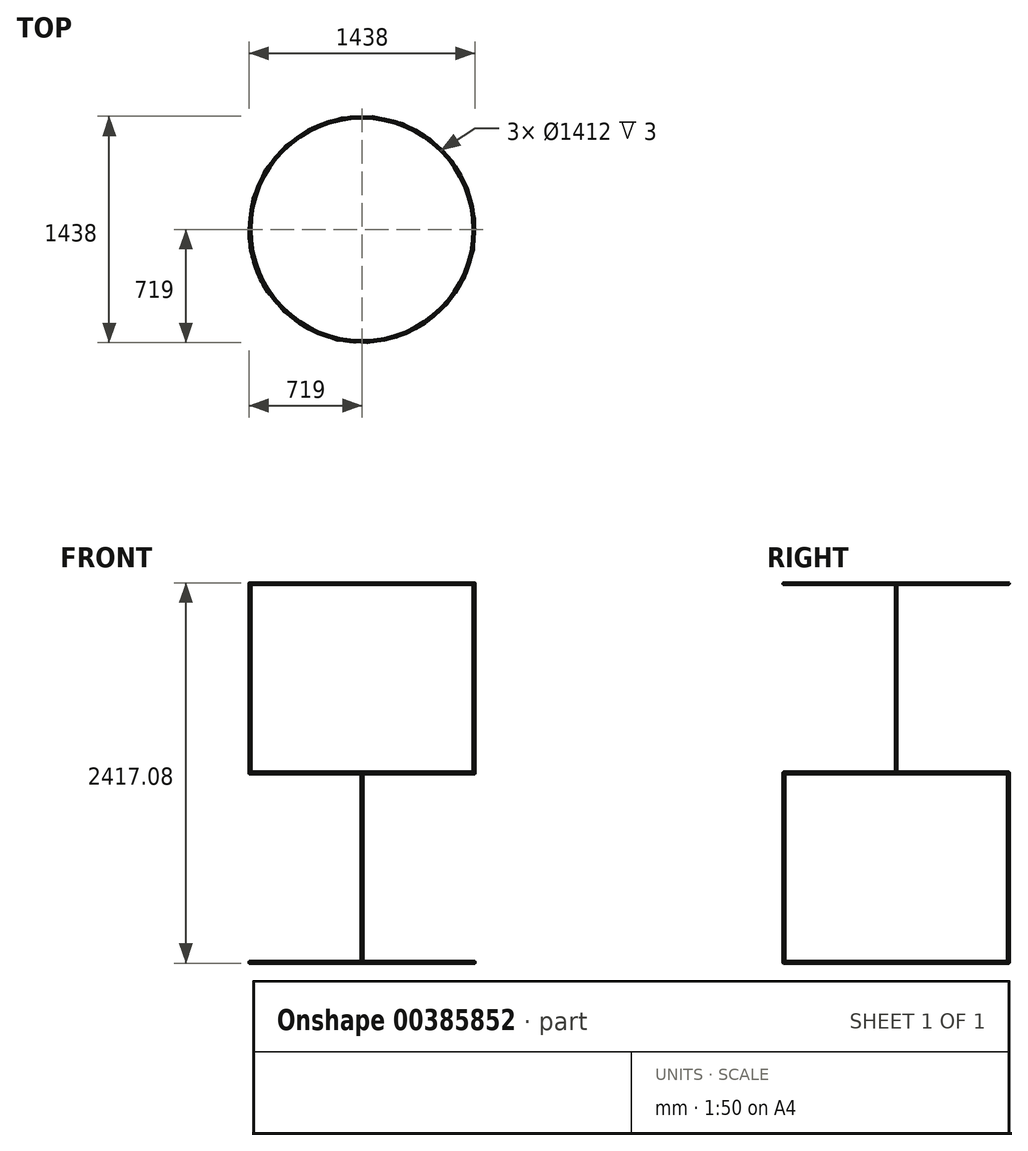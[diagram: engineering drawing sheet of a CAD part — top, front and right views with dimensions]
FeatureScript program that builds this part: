
annotation { "Feature Type Name" : "Feature", "Feature Type Description" : "" }
export const myFeature = defineFeature(function(context is Context, id is Id, definition is map)
    precondition{}
    {
        {
            var Q0;
            Q0=qCreatedBy(makeId("Front.planeOp"),FACE);
            var sketch = newSketch(context, id + "F0", { "sketchPlane" : qUnion([Q0])});
            skLineSegment(sketch, "E0", {"start": v(0, 0) * mm, "end": v(716, 0) * mm, "construction": true});
            skLineSegment(sketch, "E1", {"start": v(0, 0) * mm, "end": v(0, 347.59) * mm, "construction": true});
            skLineSegment(sketch, "E2", {"start": v(706, 1.5) * mm, "end": v(706, -1.5) * mm});
            skLineSegment(sketch, "E3", {"start": v(706, 1.5) * mm, "end": v(709, 1.5) * mm});
            skLineSegment(sketch, "E4", {"start": v(709, 1.5) * mm, "end": v(716, 5.54) * mm});
            skLineSegment(sketch, "E5", {"start": v(716, 0) * mm, "end": v(716, 5.54) * mm, "construction": true});
            skLineSegment(sketch, "E6", {"start": v(716, 0) * mm, "end": v(719, 0) * mm, "construction": true});
            skLineSegment(sketch, "E7.MirrorCS", {"start": v(706, -1.5) * mm, "end": v(709, -1.5) * mm});
            skLineSegment(sketch, "E8.MirrorCS", {"start": v(709, -1.5) * mm, "end": v(716, -5.54) * mm});
            skArc(sketch, "E9", {"start": v(716, -5.54) * mm, "mid": v(719, 0) * mm, "end": v(716, 5.54) * mm});
            skLineSegment(sketch, "E10.0.1.0", {"start": v(709, 1204.5) * mm, "end": v(716, 1208.54) * mm});
            skLineSegment(sketch, "E10.0.1.1", {"start": v(706, 1204.5) * mm, "end": v(709, 1204.5) * mm});
            skLineSegment(sketch, "E10.0.1.2", {"start": v(706, 1204.5) * mm, "end": v(706, 1201.5) * mm});
            skLineSegment(sketch, "E10.0.1.3", {"start": v(706, 1201.5) * mm, "end": v(709, 1201.5) * mm});
            skLineSegment(sketch, "E10.0.1.4", {"start": v(709, 1201.5) * mm, "end": v(716, 1197.46) * mm});
            skArc(sketch, "E10.0.1.5", {"start": v(716, 1197.46) * mm, "mid": v(719, 1203) * mm, "end": v(716, 1208.54) * mm});
            skLineSegment(sketch, "E10.direction1", {"start": v(709, 1.5) * mm, "end": v(734, 1.5) * mm, "construction": true});
            skLineSegment(sketch, "E10.direction2", {"start": v(709, 1.5) * mm, "end": v(709, 1204.5) * mm, "construction": true});
            skLineSegment(sketch, "E11.MirrorCS", {"start": v(706, -1201.5) * mm, "end": v(709, -1201.5) * mm});
            skLineSegment(sketch, "E12.MirrorCS", {"start": v(709, -1201.5) * mm, "end": v(716, -1197.46) * mm});
            skLineSegment(sketch, "E13.MirrorCS", {"start": v(706, -1204.5) * mm, "end": v(709, -1204.5) * mm});
            skLineSegment(sketch, "E14.MirrorCS", {"start": v(706, -1204.5) * mm, "end": v(706, -1201.5) * mm});
            skLineSegment(sketch, "E15.MirrorCS", {"start": v(709, -1204.5) * mm, "end": v(716, -1208.54) * mm});
            skArc(sketch, "E16.MirrorCS", {"start": v(716, -1197.46) * mm, "mid": v(719, -1203) * mm, "end": v(716, -1208.54) * mm});
            skSolve(sketch);
        }
        {
            var Q0;
            Q0 = qSketchRegion(id + "F0", true);
            var Q1;
            Q1=sQuery(id+"F0.wireOp",EDGE,"E1");
            revolve(context, id + "F1", {"entities" : qUnion([Q0]), "axis" : qUnion([Q1]), "revolveType" : RevolveType.FULL});
        }
        {
            var Q0;
            Q0=qCreatedBy(makeId("Top.planeOp"),FACE);
            var sketch = newSketch(context, id + "F2", { "sketchPlane" : qUnion([Q0])});
            skLineSegment(sketch, "E17", {"start": v(0, 0) * mm, "end": v(0, 716) * mm, "construction": true});
            skLineSegment(sketch, "E18", {"start": v(-1.5, 706) * mm, "end": v(1.5, 706) * mm});
            skLineSegment(sketch, "E19", {"start": v(-1.5, 706) * mm, "end": v(-1.5, 709) * mm});
            skLineSegment(sketch, "E20", {"start": v(-1.5, 709) * mm, "end": v(-5.54, 716) * mm});
            skLineSegment(sketch, "E21", {"start": v(0, 716) * mm, "end": v(-5.54, 716) * mm, "construction": true});
            skLineSegment(sketch, "E22.MirrorCS", {"start": v(1.5, 706) * mm, "end": v(1.5, 709) * mm});
            skLineSegment(sketch, "E23.MirrorCS", {"start": v(1.5, 709) * mm, "end": v(5.54, 716) * mm});
            skLineSegment(sketch, "E24", {"start": v(0, 716) * mm, "end": v(0, 719) * mm, "construction": true});
            skArc(sketch, "E25", {"start": v(5.54, 716) * mm, "mid": v(0, 719) * mm, "end": v(-5.54, 716) * mm});
            skArc(sketch, "E26.1.0", {"start": v(-716, 5.54) * mm, "mid": v(-719, 0) * mm, "end": v(-716, -5.54) * mm});
            skLineSegment(sketch, "E26.1.1", {"start": v(-709, -1.5) * mm, "end": v(-716, -5.54) * mm});
            skLineSegment(sketch, "E26.1.2", {"start": v(-709, 1.5) * mm, "end": v(-716, 5.54) * mm});
            skLineSegment(sketch, "E26.1.3", {"start": v(-706, 1.5) * mm, "end": v(-709, 1.5) * mm});
            skLineSegment(sketch, "E26.1.4", {"start": v(-706, -1.5) * mm, "end": v(-709, -1.5) * mm});
            skLineSegment(sketch, "E26.1.5", {"start": v(-706, -1.5) * mm, "end": v(-706, 1.5) * mm});
            skArc(sketch, "E26.2.0", {"start": v(-5.54, -716) * mm, "mid": v(0, -719) * mm, "end": v(5.54, -716) * mm});
            skLineSegment(sketch, "E26.2.1", {"start": v(1.5, -709) * mm, "end": v(5.54, -716) * mm});
            skLineSegment(sketch, "E26.2.2", {"start": v(-1.5, -709) * mm, "end": v(-5.54, -716) * mm});
            skLineSegment(sketch, "E26.2.3", {"start": v(-1.5, -706) * mm, "end": v(-1.5, -709) * mm});
            skLineSegment(sketch, "E26.2.4", {"start": v(1.5, -706) * mm, "end": v(1.5, -709) * mm});
            skLineSegment(sketch, "E26.2.5", {"start": v(1.5, -706) * mm, "end": v(-1.5, -706) * mm});
            skArc(sketch, "E26.3.0", {"start": v(716, -5.54) * mm, "mid": v(719, 0) * mm, "end": v(716, 5.54) * mm});
            skLineSegment(sketch, "E26.3.1", {"start": v(709, 1.5) * mm, "end": v(716, 5.54) * mm});
            skLineSegment(sketch, "E26.3.2", {"start": v(709, -1.5) * mm, "end": v(716, -5.54) * mm});
            skLineSegment(sketch, "E26.3.3", {"start": v(706, -1.5) * mm, "end": v(709, -1.5) * mm});
            skLineSegment(sketch, "E26.3.4", {"start": v(706, 1.5) * mm, "end": v(709, 1.5) * mm});
            skLineSegment(sketch, "E26.3.5", {"start": v(706, 1.5) * mm, "end": v(706, -1.5) * mm});
            skPoint(sketch, "E26.center", {"position": v(0, 0) * mm});
            skSolve(sketch);
        }
        {
            var Q0;
            Q0=makeQuery(id+"F2.imprint","IMPRINT",FACE,{"disambiguationData":[TD([[makeQuery(id+"F2.imprint","IMPRINT",EDGE,{"derivedFrom":sQuery(id+"F2.wireOp",EDGE,"E26.2.0")}),1.0]])]});
            var Q1;
            Q1=makeQuery(id+"F2.imprint","IMPRINT",FACE,{"disambiguationData":[TD([[makeQuery(id+"F2.imprint","IMPRINT",EDGE,{"derivedFrom":sQuery(id+"F2.wireOp",EDGE,"E18")}),1.0]])]});
            extrude(context, id + "F3", {"entities" : qUnion([Q0, Q1]), "operationType" : NewBodyOperationType.ADD, "oppositeDirection" : true, "depth" : 1203 * mm});
        }
        {
            var Q0;
            Q0=makeQuery(id+"F2.imprint","IMPRINT",FACE,{"disambiguationData":[TD([[makeQuery(id+"F2.imprint","IMPRINT",EDGE,{"derivedFrom":sQuery(id+"F2.wireOp",EDGE,"E26.1.0")}),1.0]])]});
            var Q1;
            Q1=makeQuery(id+"F2.imprint","IMPRINT",FACE,{"disambiguationData":[TD([[makeQuery(id+"F2.imprint","IMPRINT",EDGE,{"derivedFrom":sQuery(id+"F2.wireOp",EDGE,"E26.3.0")}),1.0]])]});
            extrude(context, id + "F4", {"entities" : qUnion([Q0, Q1]), "operationType" : NewBodyOperationType.ADD, "depth" : 1203 * mm});
        }
    });
